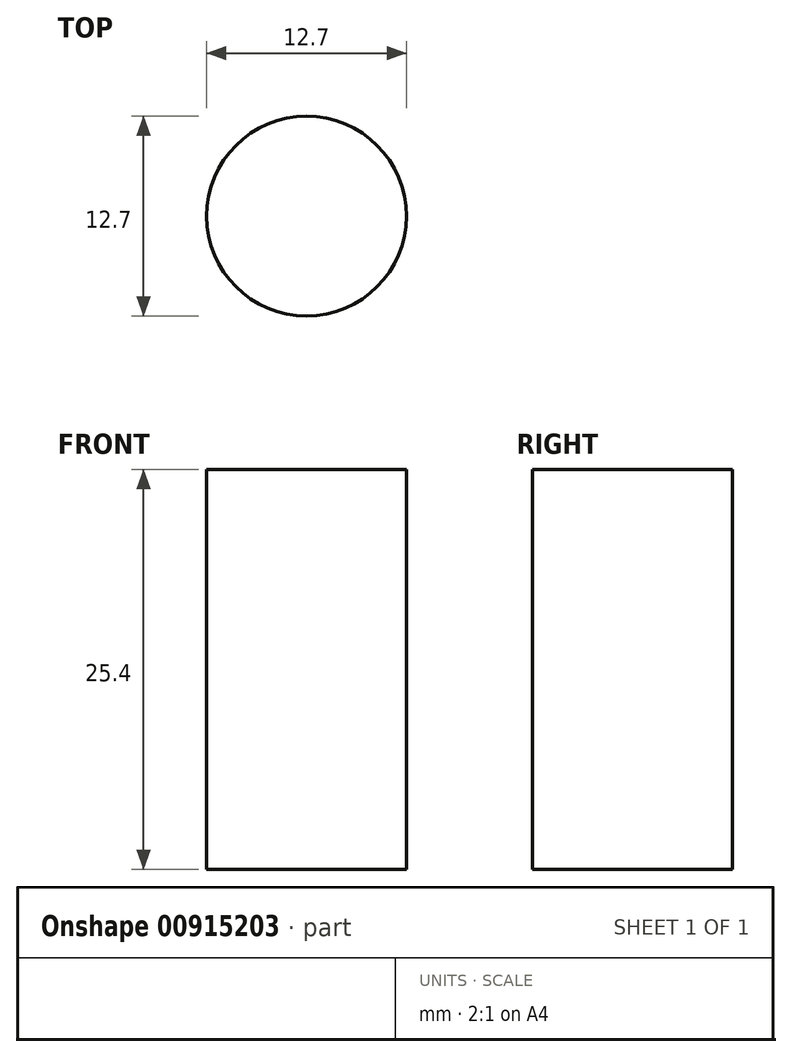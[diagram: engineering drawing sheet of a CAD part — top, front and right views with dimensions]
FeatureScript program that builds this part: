
annotation { "Feature Type Name" : "Feature", "Feature Type Description" : "" }
export const myFeature = defineFeature(function(context is Context, id is Id, definition is map)
    precondition{}
    {
        {
            var Q0;
            Q0=qCreatedBy(makeId("Top.planeOp"),FACE);
            var sketch = newSketch(context, id + "F0", { "sketchPlane" : qUnion([Q0])});
            skCircle(sketch, "E0", {"center": v(0, -0.18) * mm, "radius": 6.35 * mm});
            skSolve(sketch);
        }
        {
            var Q0;
            Q0=makeQuery(id+"F0.imprint","IMPRINT",FACE,{"disambiguationData":[TD([[makeQuery(id+"F0.imprint","IMPRINT",EDGE,{"derivedFrom":sQuery(id+"F0.wireOp",EDGE,"E0")}),1.0]])]});
            extrude(context, id + "F1", {"entities" : qUnion([Q0]), "depth" : 25.4 * mm, "offsetDistance" : 25.4 * mm});
        }
    });
